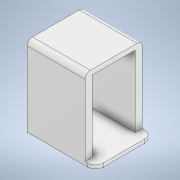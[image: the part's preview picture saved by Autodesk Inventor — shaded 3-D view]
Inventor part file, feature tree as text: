
AUTODESK INVENTOR PART (.ipt)
format: ipt  version: 2020 (Build 240168000, 168)  size: 135,680 bytes
history: native  units: in
note: dims shown in document units (in); Inventor stores cm internally (conversion verified against a paired STEP export)
features: extrude x4, fillet x3, sketch x1
ambient origin geometry x8: Origin, YZ Plane, XZ Plane, XY Plane, X Axis, Y Axis, Z Axis, Center Point
bodies: Solid1 (feature_tree)
feature tree (8):
  sketch  "Sketch1"  dims[d0=15.625in d1=11.0in d2=13.75in d3=8.25in d4=11.125in d5=0.0in d6=2.0in d7=0.0in d8=7.5in d9=0.0in d10=9.75in d11=0.0in d12=1.0in d13=0.25in d14=1.5in]
  extrude  "Extrusion1"  Depth=11.0in
  extrude  "Extrusion2"  Depth=13.75in
  extrude  "Extrusion3"  Depth=8.25in
  extrude  "Extrusion4"  Depth=11.125in TaperAngle=0.0deg
  fillet  "Fillet3"  Radius=2.0in
  fillet  "Fillet1"  Radius=7.5in
  fillet  "Fillet2"  Radius=9.75in
